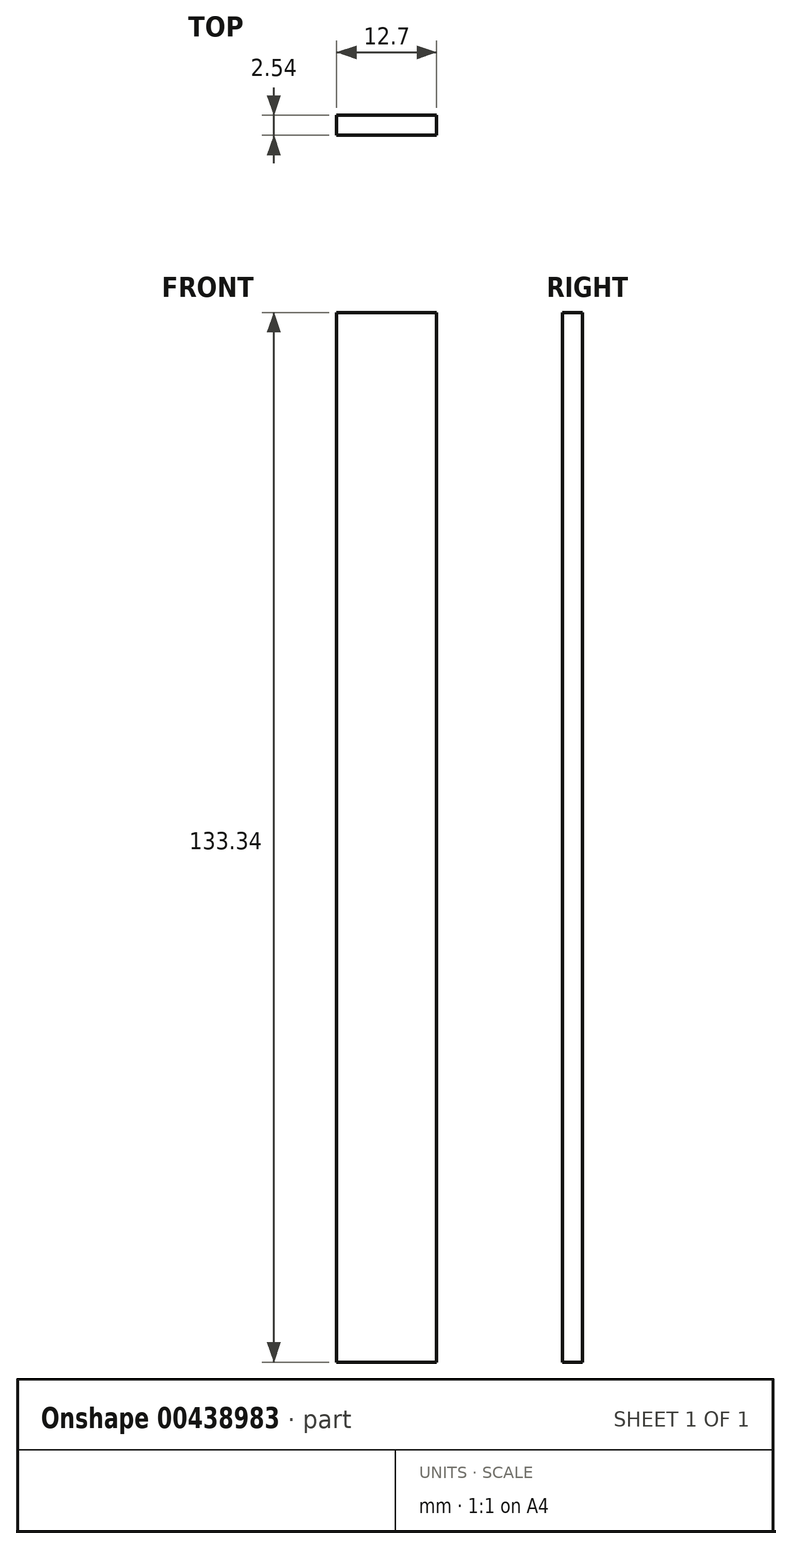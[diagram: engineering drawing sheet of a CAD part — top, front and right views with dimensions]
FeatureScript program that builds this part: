
annotation { "Feature Type Name" : "Feature", "Feature Type Description" : "" }
export const myFeature = defineFeature(function(context is Context, id is Id, definition is map)
    precondition{}
    {
        {
            var Q0;
            Q0=qCreatedBy(makeId("Front.planeOp"),FACE);
            var sketch = newSketch(context, id + "F0", { "sketchPlane" : qUnion([Q0])});
            skLineSegment(sketch, "E0.bottom", {"start": v(6.35, -66.68) * mm, "end": v(-6.35, -66.68) * mm});
            skLineSegment(sketch, "E0.top", {"start": v(6.35, 66.68) * mm, "end": v(-6.35, 66.68) * mm});
            skLineSegment(sketch, "E0.left", {"start": v(6.35, -66.68) * mm, "end": v(6.35, 66.68) * mm});
            skLineSegment(sketch, "E0.right", {"start": v(-6.35, -66.68) * mm, "end": v(-6.35, 66.68) * mm});
            skPoint(sketch, "E0.middle", {"position": v(0, 0) * mm});
            skSolve(sketch);
        }
        {
            var Q0;
            Q0 = qSketchRegion(id + "F0", true);
            extrude(context, id + "F1", {"entities" : qUnion([Q0]), "depth" : 2.54 * mm});
        }
    });
